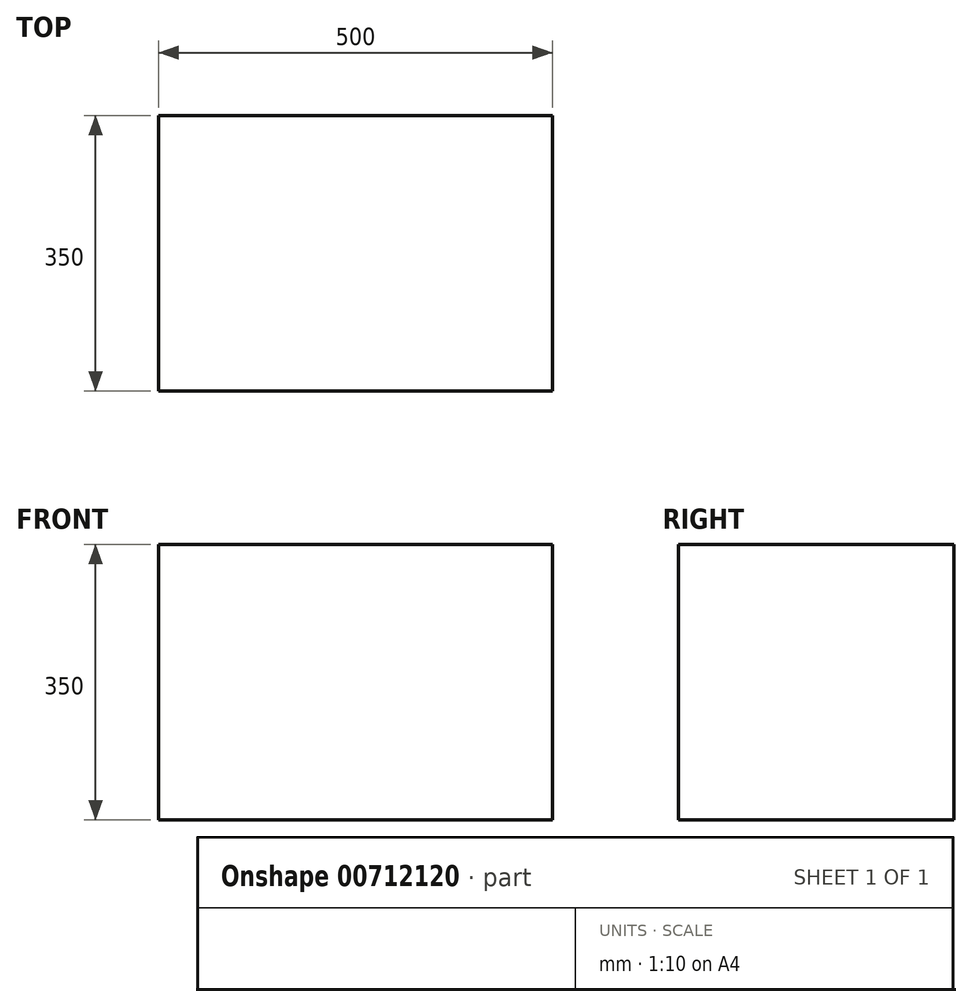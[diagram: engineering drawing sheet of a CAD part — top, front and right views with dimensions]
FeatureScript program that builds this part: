
annotation { "Feature Type Name" : "Feature", "Feature Type Description" : "" }
export const myFeature = defineFeature(function(context is Context, id is Id, definition is map)
    precondition{}
    {
        {
            var Q0;
            Q0=qCreatedBy(makeId("Top.planeOp"),FACE);
            var sketch = newSketch(context, id + "F0", { "sketchPlane" : qUnion([Q0])});
            skLineSegment(sketch, "E0.bottom", {"start": v(-250, 175) * mm, "end": v(250, 175) * mm});
            skLineSegment(sketch, "E0.top", {"start": v(-250, -175) * mm, "end": v(250, -175) * mm});
            skLineSegment(sketch, "E0.left", {"start": v(-250, 175) * mm, "end": v(-250, -175) * mm});
            skLineSegment(sketch, "E0.right", {"start": v(250, 175) * mm, "end": v(250, -175) * mm});
            skPoint(sketch, "E0.middle", {"position": v(0, 0) * mm});
            skSolve(sketch);
        }
        {
            var Q0;
            Q0=makeQuery(id+"F0.imprint","IMPRINT",FACE,{"disambiguationData":[TD([[makeQuery(id+"F0.imprint","IMPRINT",EDGE,{"derivedFrom":sQuery(id+"F0.wireOp",EDGE,"E0.bottom")}),-1.0]])]});
            extrude(context, id + "F1", {"entities" : qUnion([Q0]), "depth" : 350 * mm, "offsetDistance" : 25 * mm});
        }
    });
